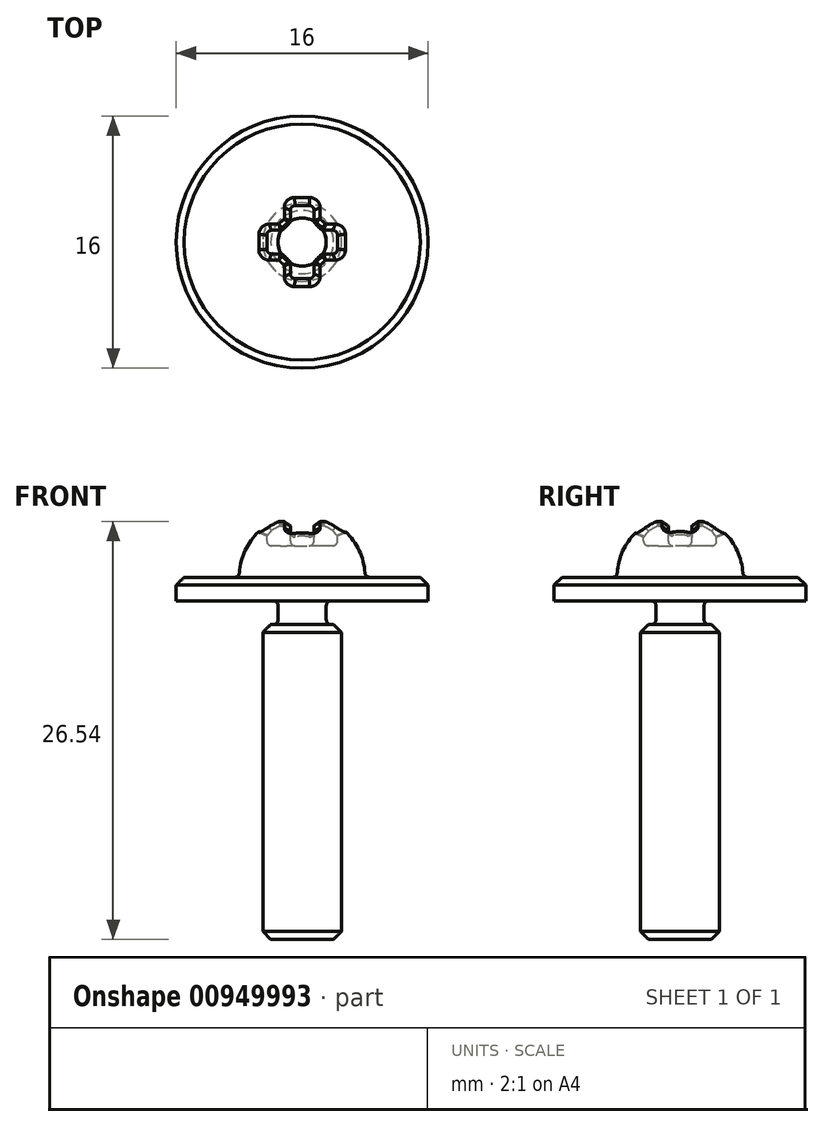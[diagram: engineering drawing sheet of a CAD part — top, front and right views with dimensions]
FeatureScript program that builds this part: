
annotation { "Feature Type Name" : "Feature", "Feature Type Description" : "" }
export const myFeature = defineFeature(function(context is Context, id is Id, definition is map)
    precondition{}
    {
        {
            var Q0;
            Q0=qCreatedBy(makeId("Front.planeOp"),FACE);
            var sketch = newSketch(context, id + "F0", { "sketchPlane" : qUnion([Q0])});
            skFitSpline(sketch, "E0", {"points": [v(-55.22, 0) * mm, v(-13.92, -24.73) * mm, v(25.15, 14.59) * mm, v(53.35, 0) * mm], "startDerivative": vector(122.47, -129.15) * mm, "endDerivative": vector(99.91, -99.13) * mm});
            skSolve(sketch);
        }
        {
            var Q0;
            Q0=qCreatedBy(makeId("Front.planeOp"),FACE);
            var sketch = newSketch(context, id + "F1", { "sketchPlane" : qUnion([Q0])});
            skLineSegment(sketch, "E1", {"start": v(0, 0) * mm, "end": v(2.5, 0) * mm});
            skLineSegment(sketch, "E2", {"start": v(2.5, 0) * mm, "end": v(2.5, 20) * mm});
            skLineSegment(sketch, "E3", {"start": v(2.5, 20) * mm, "end": v(1.53, 20) * mm});
            skLineSegment(sketch, "E4", {"start": v(1.53, 20) * mm, "end": v(1.53, 21.5) * mm});
            skLineSegment(sketch, "E5", {"start": v(8, 21.5) * mm, "end": v(1.53, 21.5) * mm});
            skLineSegment(sketch, "E6", {"start": v(8, 21.5) * mm, "end": v(8, 21.5) * mm});
            skLineSegment(sketch, "E7", {"start": v(8, 21.5) * mm, "end": v(8, 23) * mm});
            skLineSegment(sketch, "E8", {"start": v(8, 23) * mm, "end": v(4, 23) * mm});
            skArc(sketch, "E9", {"start": v(4, 23) * mm, "mid": v(2.83, 25.83) * mm, "end": v(0, 27) * mm});
            skLineSegment(sketch, "E10", {"start": v(0, 27) * mm, "end": v(0, 0) * mm});
            skSolve(sketch);
        }
        {
            var Q0;
            Q0=makeQuery(id+"F1.imprint","IMPRINT",FACE,{"disambiguationData":[TD([[makeQuery(id+"F1.imprint","IMPRINT",EDGE,{"derivedFrom":sQuery(id+"F1.wireOp",EDGE,"E1")}),1.0]])]});
            var Q1;
            Q1=sQuery(id+"F1.wireOp",EDGE,"E10");
            revolve(context, id + "F2", {"surfaceOperationType" : NewSurfaceOperationType.NEW, "entities" : qUnion([Q0]), "axis" : qUnion([Q1]), "revolveType" : RevolveType.FULL});
        }
        {
            var Q0;
            Q0=makeQuery(id+"F2.opRevolve","SWEPT_EDGE",EDGE,{"disambiguationData":[OSD([sQuery(id+"F1.wireOp",EDGE,"E1"),sQuery(id+"F1.wireOp",EDGE,"E2")])]});
            var Q1;
            Q1=makeQuery(id+"F2.opRevolve","SWEPT_EDGE",EDGE,{"disambiguationData":[OSD([sQuery(id+"F1.wireOp",EDGE,"E7"),sQuery(id+"F1.wireOp",EDGE,"E8")])]});
            var Q2;
            Q2=makeQuery(id+"F2.opRevolve","SWEPT_EDGE",EDGE,{"disambiguationData":[OSD([sQuery(id+"F1.wireOp",EDGE,"E2"),sQuery(id+"F1.wireOp",EDGE,"E3")])]});
            chamfer(context, id + "F3", {"entities" : qUnion([Q0, Q1, Q2]), "width" : 0.5 * mm, "tangentPropagation" : true});
        }
        {
            var Q0;
            Q0=makeQuery(id+"F2.opRevolve","SWEPT_EDGE",EDGE,{"disambiguationData":[OSD([sQuery(id+"F1.wireOp",EDGE,"E8"),sQuery(id+"F1.wireOp",EDGE,"E9")])]});
            var Q1;
            Q1=makeQuery(id+"F2.opRevolve","SWEPT_EDGE",EDGE,{"disambiguationData":[OSD([sQuery(id+"F1.wireOp",EDGE,"E4"),sQuery(id+"F1.wireOp",EDGE,"E5")])]});
            var Q2;
            Q2=makeQuery(id+"F2.opRevolve","SWEPT_EDGE",EDGE,{"disambiguationData":[OSD([sQuery(id+"F1.wireOp",EDGE,"E3"),sQuery(id+"F1.wireOp",EDGE,"E4")])]});
            fillet(context, id + "F4", {"entities" : qUnion([Q0, Q1, Q2]), "tangentPropagation" : true, "radius" : 0.3 * mm, "defaultsChanged" : true, "vertexSettings" : [], "allowEdgeOverflow" : false});
        }
        {
            var Q0;
            Q0=qCreatedBy(makeId("Top.planeOp"),FACE);
            var Q1;
            Q1=sQuery(id+"F1.wireOp",VERTEX,"E9.end");
            cPlane(context, id + "F5", {"entities" : qUnion([Q0, Q1]), "cplaneType" : CPlaneType.PLANE_POINT, "offset" : 25.4 * mm, "width" : 152.4 * mm, "height" : 152.4 * mm});
        }
        {
            var Q0;
            Q0=qCreatedBy(id+"F5.planeOp",FACE);
            var sketch = newSketch(context, id + "F6", { "sketchPlane" : qUnion([Q0])});
            skCircle(sketch, "E11.cCircle", {"center": v(0, 0) * mm, "radius": 2.68 * mm, "construction": true});
            skLineSegment(sketch, "E11.0", {"start": v(2.68, 0) * mm, "end": v(1.34, -2.32) * mm, "construction": true});
            skLineSegment(sketch, "E11.1", {"start": v(1.34, -2.32) * mm, "end": v(-1.34, -2.32) * mm, "construction": true});
            skLineSegment(sketch, "E11.2", {"start": v(-1.34, -2.32) * mm, "end": v(-2.68, 0) * mm, "construction": true});
            skLineSegment(sketch, "E11.3", {"start": v(-2.68, 0) * mm, "end": v(-1.34, 2.32) * mm, "construction": true});
            skLineSegment(sketch, "E11.4", {"start": v(-1.34, 2.32) * mm, "end": v(1.34, 2.32) * mm, "construction": true});
            skLineSegment(sketch, "E11.5", {"start": v(1.34, 2.32) * mm, "end": v(2.68, 0) * mm, "construction": true});
            skLineSegment(sketch, "E12", {"start": v(0.75, 2.32) * mm, "end": v(0.75, 0.75) * mm});
            skLineSegment(sketch, "E13", {"start": v(0.75, 0.75) * mm, "end": v(2.25, 0.75) * mm});
            skLineSegment(sketch, "E14", {"start": v(2.25, 0.75) * mm, "end": v(2.25, -0.75) * mm});
            skLineSegment(sketch, "E15", {"start": v(2.25, -0.75) * mm, "end": v(0.75, -0.75) * mm});
            skLineSegment(sketch, "E16", {"start": v(0.75, -0.75) * mm, "end": v(0.75, -2.32) * mm});
            skLineSegment(sketch, "E17", {"start": v(0.75, 2.32) * mm, "end": v(0, 2.32) * mm});
            skLineSegment(sketch, "E18", {"start": v(0.75, -2.32) * mm, "end": v(0, -2.32) * mm});
            skLineSegment(sketch, "E19", {"start": v(0, 2.32) * mm, "end": v(0, -2.32) * mm, "construction": true});
            skLineSegment(sketch, "E20.MirrorCS", {"start": v(-0.75, 2.32) * mm, "end": v(0, 2.32) * mm});
            skLineSegment(sketch, "E21.MirrorCS", {"start": v(-0.75, 2.32) * mm, "end": v(-0.75, 0.75) * mm});
            skLineSegment(sketch, "E22.MirrorCS", {"start": v(-0.75, 0.75) * mm, "end": v(-2.25, 0.75) * mm});
            skLineSegment(sketch, "E23.MirrorCS", {"start": v(-2.25, 0.75) * mm, "end": v(-2.25, -0.75) * mm});
            skLineSegment(sketch, "E24.MirrorCS", {"start": v(-2.25, -0.75) * mm, "end": v(-0.75, -0.75) * mm});
            skLineSegment(sketch, "E25.MirrorCS", {"start": v(-0.75, -0.75) * mm, "end": v(-0.75, -2.32) * mm});
            skLineSegment(sketch, "E26.MirrorCS", {"start": v(-0.75, -2.32) * mm, "end": v(0, -2.32) * mm});
            skSolve(sketch);
        }
        {
            var Q0;
            Q0 = qSketchRegion(id + "F6", true);
            extrude(context, id + "F7", {"entities" : qUnion([Q0]), "operationType" : NewBodyOperationType.REMOVE, "oppositeDirection" : true, "depth" : 2 * mm, "offsetDistance" : 25.4 * mm});
        }
        {
            var Q0;
            Q0=makeQuery(id+"F7.boolean.opBoolean","COPY",EDGE,{"derivedFrom":makeQuery(id+"F7.opExtrude","SWEPT_EDGE",EDGE,{"disambiguationData":[OSD([sQuery(id+"F6.wireOp",EDGE,"E21.MirrorCS"),sQuery(id+"F6.wireOp",EDGE,"E22.MirrorCS")])]})});
            var Q1;
            Q1=makeQuery(id+"F7.boolean.opBoolean","COPY",EDGE,{"derivedFrom":makeQuery(id+"F7.opExtrude","SWEPT_EDGE",EDGE,{"disambiguationData":[OSD([sQuery(id+"F6.wireOp",EDGE,"E12"),sQuery(id+"F6.wireOp",EDGE,"E13")])]})});
            var Q2;
            Q2=makeQuery(id+"F7.boolean.opBoolean","COPY",EDGE,{"derivedFrom":makeQuery(id+"F7.opExtrude","SWEPT_EDGE",EDGE,{"disambiguationData":[OSD([sQuery(id+"F6.wireOp",EDGE,"E24.MirrorCS"),sQuery(id+"F6.wireOp",EDGE,"E25.MirrorCS")])]})});
            var Q3;
            Q3=makeQuery(id+"F7.boolean.opBoolean","COPY",EDGE,{"derivedFrom":makeQuery(id+"F7.opExtrude","SWEPT_EDGE",EDGE,{"disambiguationData":[OSD([sQuery(id+"F6.wireOp",EDGE,"E15"),sQuery(id+"F6.wireOp",EDGE,"E16")])]})});
            chamfer(context, id + "F8", {"entities" : qUnion([Q0, Q1, Q2, Q3]), "width" : 0.5 * mm, "tangentPropagation" : true});
        }
        {
            var Q0;
            Q0=makeQuery(id+"F7.boolean.opBoolean","COPY",EDGE,{"derivedFrom":makeQuery(id+"F7.opExtrude","SWEPT_EDGE",EDGE,{"disambiguationData":[OSD([sQuery(id+"F6.wireOp",EDGE,"E22.MirrorCS"),sQuery(id+"F6.wireOp",EDGE,"E23.MirrorCS")])]})});
            var Q1;
            {var subQ0=sQuery(id+"F6.wireOp",EDGE,"E22.MirrorCS");Q1=makeQuery(id+"F8.opChamfer","BLEND_EDGE",EDGE,{"blendedFrom":[makeQuery(id+"F7.boolean.opBoolean","COPY",EDGE,{"derivedFrom":makeQuery(id+"F7.opExtrude","SWEPT_EDGE",EDGE,{"disambiguationData":[OSD([sQuery(id+"F6.wireOp",EDGE,"E21.MirrorCS"),subQ0])]})}),makeQuery(id+"F7.boolean.opBoolean","COPY",FACE,{"derivedFrom":makeQuery(id+"F7.opExtrude","SWEPT_FACE",FACE,{"disambiguationData":[OSD([subQ0])]})})],"blendedInto":[makeQuery(id+"F7.boolean.opBoolean","COPY",FACE,{"derivedFrom":makeQuery(id+"F7.opExtrude","SWEPT_FACE",FACE,{"disambiguationData":[OSD([subQ0])]})})]});}
            var Q2;
            {var subQ0=sQuery(id+"F6.wireOp",EDGE,"E21.MirrorCS");Q2=makeQuery(id+"F8.opChamfer","BLEND_EDGE",EDGE,{"blendedFrom":[makeQuery(id+"F7.boolean.opBoolean","COPY",EDGE,{"derivedFrom":makeQuery(id+"F7.opExtrude","SWEPT_EDGE",EDGE,{"disambiguationData":[OSD([subQ0,sQuery(id+"F6.wireOp",EDGE,"E22.MirrorCS")])]})}),makeQuery(id+"F7.boolean.opBoolean","COPY",FACE,{"derivedFrom":makeQuery(id+"F7.opExtrude","SWEPT_FACE",FACE,{"disambiguationData":[OSD([subQ0])]})})],"blendedInto":[makeQuery(id+"F7.boolean.opBoolean","COPY",FACE,{"derivedFrom":makeQuery(id+"F7.opExtrude","SWEPT_FACE",FACE,{"disambiguationData":[OSD([subQ0])]})})]});}
            var Q3;
            Q3=makeQuery(id+"F7.boolean.opBoolean","COPY",EDGE,{"derivedFrom":makeQuery(id+"F7.opExtrude","SWEPT_EDGE",EDGE,{"disambiguationData":[OSD([sQuery(id+"F6.wireOp",EDGE,"E20.MirrorCS"),sQuery(id+"F6.wireOp",EDGE,"E21.MirrorCS")])]})});
            var Q4;
            Q4=makeQuery(id+"F7.boolean.opBoolean","COPY",EDGE,{"derivedFrom":makeQuery(id+"F7.opExtrude","SWEPT_EDGE",EDGE,{"disambiguationData":[OSD([sQuery(id+"F6.wireOp",EDGE,"E23.MirrorCS"),sQuery(id+"F6.wireOp",EDGE,"E24.MirrorCS")])]})});
            var Q5;
            {var subQ0=sQuery(id+"F6.wireOp",EDGE,"E24.MirrorCS");Q5=makeQuery(id+"F8.opChamfer","BLEND_EDGE",EDGE,{"blendedFrom":[makeQuery(id+"F7.boolean.opBoolean","COPY",EDGE,{"derivedFrom":makeQuery(id+"F7.opExtrude","SWEPT_EDGE",EDGE,{"disambiguationData":[OSD([subQ0,sQuery(id+"F6.wireOp",EDGE,"E25.MirrorCS")])]})}),makeQuery(id+"F7.boolean.opBoolean","COPY",FACE,{"derivedFrom":makeQuery(id+"F7.opExtrude","SWEPT_FACE",FACE,{"disambiguationData":[OSD([subQ0])]})})],"blendedInto":[makeQuery(id+"F7.boolean.opBoolean","COPY",FACE,{"derivedFrom":makeQuery(id+"F7.opExtrude","SWEPT_FACE",FACE,{"disambiguationData":[OSD([subQ0])]})})]});}
            var Q6;
            {var subQ0=sQuery(id+"F6.wireOp",EDGE,"E25.MirrorCS");Q6=makeQuery(id+"F8.opChamfer","BLEND_EDGE",EDGE,{"blendedFrom":[makeQuery(id+"F7.boolean.opBoolean","COPY",EDGE,{"derivedFrom":makeQuery(id+"F7.opExtrude","SWEPT_EDGE",EDGE,{"disambiguationData":[OSD([sQuery(id+"F6.wireOp",EDGE,"E24.MirrorCS"),subQ0])]})}),makeQuery(id+"F7.boolean.opBoolean","COPY",FACE,{"derivedFrom":makeQuery(id+"F7.opExtrude","SWEPT_FACE",FACE,{"disambiguationData":[OSD([subQ0])]})})],"blendedInto":[makeQuery(id+"F7.boolean.opBoolean","COPY",FACE,{"derivedFrom":makeQuery(id+"F7.opExtrude","SWEPT_FACE",FACE,{"disambiguationData":[OSD([subQ0])]})})]});}
            var Q7;
            Q7=makeQuery(id+"F7.boolean.opBoolean","COPY",EDGE,{"derivedFrom":makeQuery(id+"F7.opExtrude","SWEPT_EDGE",EDGE,{"disambiguationData":[OSD([sQuery(id+"F6.wireOp",EDGE,"E25.MirrorCS"),sQuery(id+"F6.wireOp",EDGE,"E26.MirrorCS")])]})});
            var Q8;
            Q8=makeQuery(id+"F7.boolean.opBoolean","COPY",EDGE,{"derivedFrom":makeQuery(id+"F7.opExtrude","SWEPT_EDGE",EDGE,{"disambiguationData":[OSD([sQuery(id+"F6.wireOp",EDGE,"E16"),sQuery(id+"F6.wireOp",EDGE,"E18")])]})});
            var Q9;
            {var subQ0=sQuery(id+"F6.wireOp",EDGE,"E16");Q9=makeQuery(id+"F8.opChamfer","BLEND_EDGE",EDGE,{"blendedFrom":[makeQuery(id+"F7.boolean.opBoolean","COPY",EDGE,{"derivedFrom":makeQuery(id+"F7.opExtrude","SWEPT_EDGE",EDGE,{"disambiguationData":[OSD([sQuery(id+"F6.wireOp",EDGE,"E15"),subQ0])]})}),makeQuery(id+"F7.boolean.opBoolean","COPY",FACE,{"derivedFrom":makeQuery(id+"F7.opExtrude","SWEPT_FACE",FACE,{"disambiguationData":[OSD([subQ0])]})})],"blendedInto":[makeQuery(id+"F7.boolean.opBoolean","COPY",FACE,{"derivedFrom":makeQuery(id+"F7.opExtrude","SWEPT_FACE",FACE,{"disambiguationData":[OSD([subQ0])]})})]});}
            var Q10;
            {var subQ0=sQuery(id+"F6.wireOp",EDGE,"E15");Q10=makeQuery(id+"F8.opChamfer","BLEND_EDGE",EDGE,{"blendedFrom":[makeQuery(id+"F7.boolean.opBoolean","COPY",EDGE,{"derivedFrom":makeQuery(id+"F7.opExtrude","SWEPT_EDGE",EDGE,{"disambiguationData":[OSD([subQ0,sQuery(id+"F6.wireOp",EDGE,"E16")])]})}),makeQuery(id+"F7.boolean.opBoolean","COPY",FACE,{"derivedFrom":makeQuery(id+"F7.opExtrude","SWEPT_FACE",FACE,{"disambiguationData":[OSD([subQ0])]})})],"blendedInto":[makeQuery(id+"F7.boolean.opBoolean","COPY",FACE,{"derivedFrom":makeQuery(id+"F7.opExtrude","SWEPT_FACE",FACE,{"disambiguationData":[OSD([subQ0])]})})]});}
            var Q11;
            Q11=makeQuery(id+"F7.boolean.opBoolean","COPY",EDGE,{"derivedFrom":makeQuery(id+"F7.opExtrude","SWEPT_EDGE",EDGE,{"disambiguationData":[OSD([sQuery(id+"F6.wireOp",EDGE,"E14"),sQuery(id+"F6.wireOp",EDGE,"E15")])]})});
            var Q12;
            {var subQ0=sQuery(id+"F6.wireOp",EDGE,"E13");Q12=makeQuery(id+"F8.opChamfer","BLEND_EDGE",EDGE,{"blendedFrom":[makeQuery(id+"F7.boolean.opBoolean","COPY",EDGE,{"derivedFrom":makeQuery(id+"F7.opExtrude","SWEPT_EDGE",EDGE,{"disambiguationData":[OSD([sQuery(id+"F6.wireOp",EDGE,"E12"),subQ0])]})}),makeQuery(id+"F7.boolean.opBoolean","COPY",FACE,{"derivedFrom":makeQuery(id+"F7.opExtrude","SWEPT_FACE",FACE,{"disambiguationData":[OSD([subQ0])]})})],"blendedInto":[makeQuery(id+"F7.boolean.opBoolean","COPY",FACE,{"derivedFrom":makeQuery(id+"F7.opExtrude","SWEPT_FACE",FACE,{"disambiguationData":[OSD([subQ0])]})})]});}
            var Q13;
            Q13=makeQuery(id+"F7.boolean.opBoolean","COPY",EDGE,{"derivedFrom":makeQuery(id+"F7.opExtrude","SWEPT_EDGE",EDGE,{"disambiguationData":[OSD([sQuery(id+"F6.wireOp",EDGE,"E13"),sQuery(id+"F6.wireOp",EDGE,"E14")])]})});
            var Q14;
            {var subQ0=sQuery(id+"F6.wireOp",EDGE,"E12");Q14=makeQuery(id+"F8.opChamfer","BLEND_EDGE",EDGE,{"blendedFrom":[makeQuery(id+"F7.boolean.opBoolean","COPY",EDGE,{"derivedFrom":makeQuery(id+"F7.opExtrude","SWEPT_EDGE",EDGE,{"disambiguationData":[OSD([subQ0,sQuery(id+"F6.wireOp",EDGE,"E13")])]})}),makeQuery(id+"F7.boolean.opBoolean","COPY",FACE,{"derivedFrom":makeQuery(id+"F7.opExtrude","SWEPT_FACE",FACE,{"disambiguationData":[OSD([subQ0])]})})],"blendedInto":[makeQuery(id+"F7.boolean.opBoolean","COPY",FACE,{"derivedFrom":makeQuery(id+"F7.opExtrude","SWEPT_FACE",FACE,{"disambiguationData":[OSD([subQ0])]})})]});}
            var Q15;
            Q15=makeQuery(id+"F7.boolean.opBoolean","COPY",EDGE,{"derivedFrom":makeQuery(id+"F7.opExtrude","SWEPT_EDGE",EDGE,{"disambiguationData":[OSD([sQuery(id+"F6.wireOp",EDGE,"E12"),sQuery(id+"F6.wireOp",EDGE,"E17")])]})});
            fillet(context, id + "F9", {"entities" : qUnion([Q0, Q1, Q2, Q3, Q4, Q5, Q6, Q7, Q8, Q9, Q10, Q11, Q12, Q13, Q14, Q15]), "tangentPropagation" : true, "radius" : 0.3 * mm, "defaultsChanged" : true, "vertexSettings" : [], "allowEdgeOverflow" : false});
        }
        {
            var Q0;
            Q0=makeQuery(id+"F7.boolean.opBoolean","INTERSECT",EDGE,{"derivedFrom":[makeQuery(id+"F2.opRevolve","SWEPT_FACE",FACE,{"disambiguationData":[OSD([sQuery(id+"F1.wireOp",EDGE,"E9")])]}),makeQuery(id+"F7.opExtrude","SWEPT_FACE",FACE,{"disambiguationData":[OSD([sQuery(id+"F6.wireOp",EDGE,"E23.MirrorCS")])]})]});
            chamfer(context, id + "F10", {"entities" : qUnion([Q0]), "width" : 0.3 * mm, "tangentPropagation" : true});
        }
        {
            var Q0;
            Q0=makeQuery(id+"F7.boolean.opBoolean","COPY",EDGE,{"derivedFrom":makeQuery(id+"F7.opExtrude","CAP_EDGE",EDGE,{"disambiguationData":[OSD([sQuery(id+"F6.wireOp",EDGE,"E23.MirrorCS")])],"isStart":false})});
            fillet(context, id + "F11", {"entities" : qUnion([Q0]), "tangentPropagation" : true, "radius" : 0.3 * mm, "defaultsChanged" : true, "vertexSettings" : [], "allowEdgeOverflow" : false});
        }
    });
